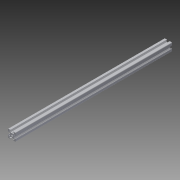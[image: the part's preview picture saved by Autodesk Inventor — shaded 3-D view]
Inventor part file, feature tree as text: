
AUTODESK INVENTOR PART (.ipt)
format: ipt  version: 2013 (Build 170138000, 138)  size: 282,112 bytes
history: native  units: in
note: dims shown in document units (in); Inventor stores cm internally (conversion verified against a paired STEP export)
features: other x3, extrude x1, sketch x1
ambient origin geometry x8: Origin, YZ Plane, XZ Plane, XY Plane, X Axis, Y Axis, Z Axis, Center Point
bodies: Solid1 (feature_tree)
feature tree (5):
  other  "Blocks"
  extrude  "Extrusion1"  [1 undecoded]
  sketch  "Sketch1"  dims[d1=0.0in]
  other  "20x20"
  other  "20x20:1"
note: 1 required parameter value undecoded (feature->parameter linkage not recoverable at this tier; creation-order binding heuristic only, values carry confidence <= 0.55)
